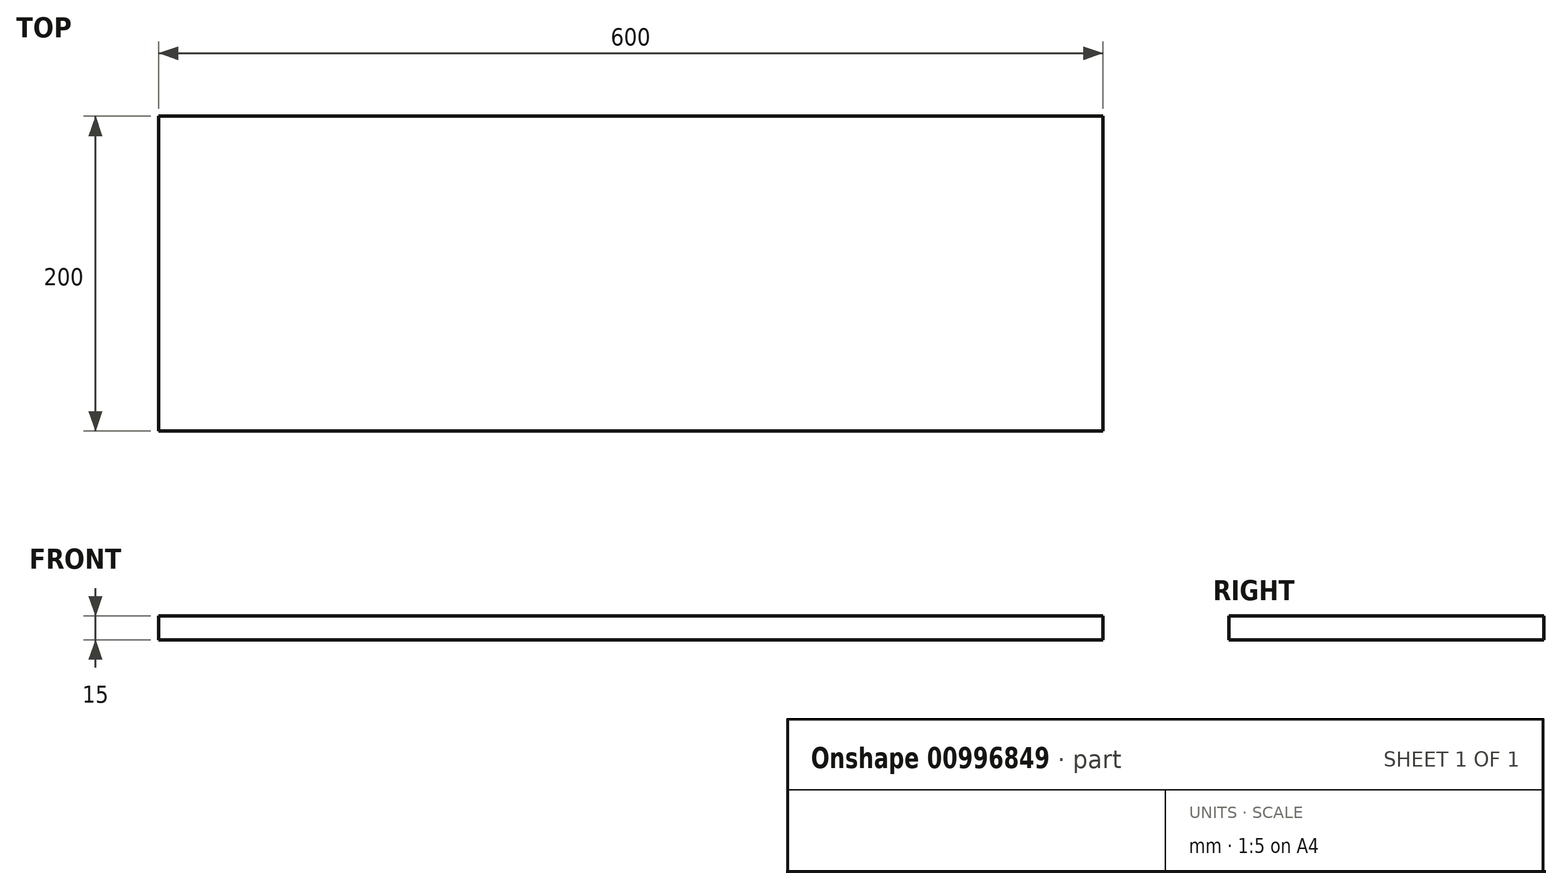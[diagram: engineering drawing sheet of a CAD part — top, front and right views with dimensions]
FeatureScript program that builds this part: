
annotation { "Feature Type Name" : "Feature", "Feature Type Description" : "" }
export const myFeature = defineFeature(function(context is Context, id is Id, definition is map)
    precondition{}
    {
        {
            var Q0;
            Q0=qCreatedBy(makeId("Front.planeOp"),FACE);
            var sketch = newSketch(context, id + "F0", { "sketchPlane" : qUnion([Q0])});
            skLineSegment(sketch, "E0.bottom", {"start": v(-300, 15) * mm, "end": v(300, 15) * mm});
            skLineSegment(sketch, "E0.top", {"start": v(-300, 0) * mm, "end": v(300, 0) * mm});
            skLineSegment(sketch, "E0.left", {"start": v(-300, 15) * mm, "end": v(-300, 0) * mm});
            skLineSegment(sketch, "E0.right", {"start": v(300, 15) * mm, "end": v(300, 0) * mm});
            skSolve(sketch);
        }
        {
            var Q0;
            Q0 = qSketchRegion(id + "F0", true);
            extrude(context, id + "F1", {"entities" : qUnion([Q0]), "oppositeDirection" : true, "depth" : 200 * mm, "offsetDistance" : 25 * mm});
        }
    });
